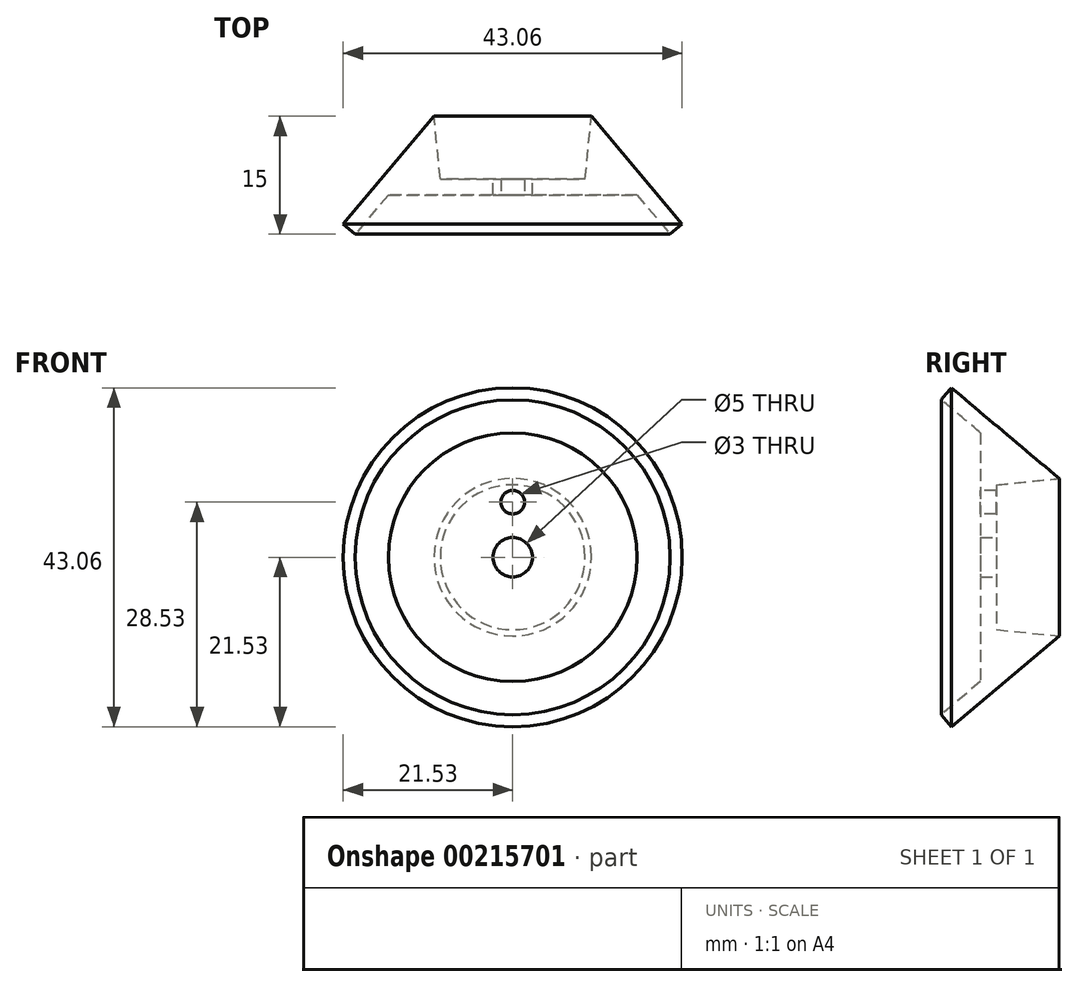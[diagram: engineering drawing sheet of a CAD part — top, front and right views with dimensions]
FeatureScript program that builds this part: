
annotation { "Feature Type Name" : "Feature", "Feature Type Description" : "" }
export const myFeature = defineFeature(function(context is Context, id is Id, definition is map)
    precondition{}
    {
        {
            var Q0;
            Q0=qCreatedBy(makeId("Top.planeOp"),FACE);
            var sketch = newSketch(context, id + "F0", { "sketchPlane" : qUnion([Q0])});
            skLineSegment(sketch, "E0", {"start": v(0, 17.67) * mm, "end": v(0, -18.99) * mm, "construction": true});
            skLineSegment(sketch, "E1", {"start": v(-10, 0) * mm, "end": v(-21.53, -13.71) * mm});
            skLineSegment(sketch, "E2", {"start": v(-21.53, -13.71) * mm, "end": v(-20, -15) * mm});
            skLineSegment(sketch, "E3", {"start": v(-20, -15) * mm, "end": v(-15.8, -10) * mm});
            skLineSegment(sketch, "E4", {"start": v(-15.8, -10) * mm, "end": v(-9, -10) * mm});
            skLineSegment(sketch, "E5", {"start": v(-9.2, -8) * mm, "end": v(-10, 0) * mm});
            skLineSegment(sketch, "E6", {"start": v(-9.2, -8) * mm, "end": v(-2.5, -8) * mm});
            skLineSegment(sketch, "E7", {"start": v(-2.5, -8) * mm, "end": v(-2.5, -10) * mm});
            skLineSegment(sketch, "E8", {"start": v(-2.5, -10) * mm, "end": v(-9, -10) * mm});
            skSolve(sketch);
        }
        {
            var Q0;
            Q0 = qSketchRegion(id + "F0", true);
            var Q1;
            Q1=sQuery(id+"F0.wireOp",EDGE,"E0");
            revolve(context, id + "F1", {"entities" : qUnion([Q0]), "axis" : qUnion([Q1]), "revolveType" : RevolveType.FULL});
        }
        {
            var Q0;
            Q0=makeQuery(id+"F1.opRevolve","SWEPT_FACE",FACE,{"disambiguationData":[OSD([sQuery(id+"F0.wireOp",EDGE,"E4"),sQuery(id+"F0.wireOp",EDGE,"E8")])]});
            var sketch = newSketch(context, id + "F2", { "sketchPlane" : qUnion([Q0])});
            skLineSegment(sketch, "E9", {"start": v(0, 2.5) * mm, "end": v(0, 15.8) * mm, "construction": true});
            skCircle(sketch, "E10", {"center": v(0, 7) * mm, "radius": 1.5 * mm});
            skSolve(sketch);
        }
        {
            var Q0;
            Q0 = qSketchRegion(id + "F2", true);
            extrude(context, id + "F3", {"entities" : qUnion([Q0]), "operationType" : NewBodyOperationType.REMOVE, "endBound" : BoundingType.THROUGH_ALL, "oppositeDirection" : true, "depth" : 25 * mm});
        }
    });
